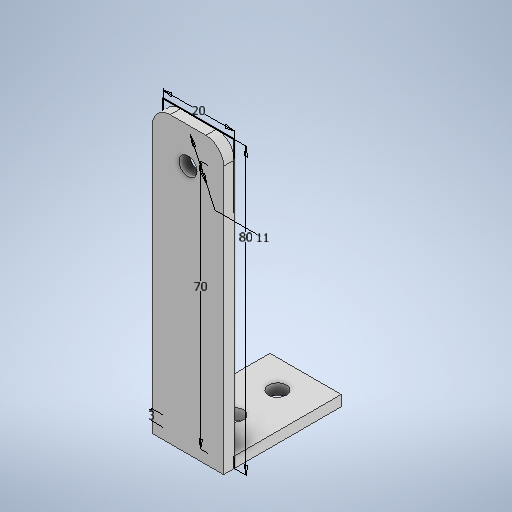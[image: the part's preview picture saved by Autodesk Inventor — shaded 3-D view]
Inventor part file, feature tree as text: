
AUTODESK INVENTOR PART (.ipt)
format: ipt  version: 2025.1 (Build 291241020, 241B)  size: 271,872 bytes
history: native  units: mm
features: extrude x3, sketch x2, fillet x1
ambient origin geometry x8: Origin, YZ Plane, XZ Plane, XY Plane, X Axis, Y Axis, Z Axis, Center Point
bodies: Solid1 (feature_tree)
feature tree (6):
  sketch  "Sketch1"  dims[d0=20.0mm d1=80.0mm d2=11.0mm]
  extrude  "Extrusion1"  Depth=80.0mm
  fillet  "Fillet1"  Radius=11.0mm
  extrude  "Extrusion2"  Depth=3.0mm TaperAngle=0.0deg
  extrude  "Extrusion3"  Depth=5.0mm
  sketch  "Sketch2"  dims[d3=70.0mm d4=3.0mm d5=0.0mm d6=5.0mm d7=3.0mm d8=30.0mm d9=0.0mm d10=5.0mm d11=5.0mm d12=0.0mm d13=0.0mm d14=0.5mm d15=0.872665mm d16=0.5mm d17=0.872665mm]
